# Revit family: Drinking_Fountain_Bottle_Filler-Murdock-H2O-To-Go-A191.8-BF_Series
name_source: partatom
category: Plumbing Fixtures
units: mm (PartAtom-declared; Revit-internal decimal feet)

## family parameters
Cut with Voids When Loaded = No
Host = Face
OmniClass Number = 23.65.70.14.11
OmniClass Title = Drinking Fountains/Coolers
Part Type = Normal
Room Calculation Point = No
Round Connector Dimension = Use Diameter
Shared = Yes

## types (6) — shared parameters
ADA = Yes
ADA Compliant = Yes
Amps = 4 A
Assembly Code = D2010800
Basin Material = Metal-Murdock-Stainless Steel
Bottle Filler Material = Stainless Steel-Murdock-Satin
CW Connection = Yes
CWFU = 1.5
Cabinet Material = Stainless Steel-Murdock-Brushed
Child ADA = No
Default Elevation = 0"
Description = Wall-Mounted, Square, Push Button Drinking Fountain with Wide Basin & H2O-to-Go!® Touchless Water Filling Station - In-Wall Refrigeration (8GPH), ADA, Stainless Steel
Finish = Metal-Murdock-18 Gage-Type 304-Bronze
Flow Rate = 1 GPM
GPH = 8.0
HW Connection = No
Height = 49 1/8"
IAPMO Compliance = Unit is certified to ANSI A117.1, Public Law 111-380 (NO-LEAD), CHSC 116875 and NSF/ANSI 61, Section 9.
Inlet Connection Diameter = 3/8"
Inlet Connection Height = 29 1/4"
Installation Instruction Link = https://www.murdockmfg.com
Installation Type = Wall Mounted
Length = 23 3/4"
Manufacturer = Murdock
Material = Metal-Murdock-Stainless Steel
Mounting Height = 27"
Mounting Height Constraint from Under Fountain = 27"
Product Documentation Link = https://www.murdockmfg.com
Product Page URL = https://www.murdockmfg.com
Pushbutton Material = Brass-Murdock-Chrome Plated
Shipping Weight = 130 lbs.
URL = http://www.murdockmfg.com
Vent Connection = No
WF1 - 1500 gallon capacity, NSF 42+53, 1 micron lead reduction filter = No
WF3 3000-Gallon Capacity, NSF 42+53, 1-Micron Lead Reduction Filter = No
WFU = 2
Warranty Information = Murdock Mfg.™ warrants that its products are free from defects in material or workmanship under normal use and service for a period of one year from date of shipment.
Waste Connection = Yes
Waste Connection Diameter = 1 1/4"
Waste Connection Height = 29 5/8"
Waste Connection Width = 4 1/4"
Water Pressure = 20-105 PSIG
Watts = 390 W
Width = 19"
cUPC Compliant = Yes
zero-valued in all types: HWFU

## per-type parameters (varying)
| type | -BCD Bottle Counter Display | 115v Plug-In Transformer | BF11 - Push Button Deck Mount H2O to Go!® Bottler Filler | BF12 - H2O-To-Go!® Sensor-Operated Water Refill Station | Bottle Filler Type | Bubbler Material | Type Comments |
| A191408F-BF11 | No | No | Yes | No | Bottle_Filler-Murdock-H2O-To-Go-BFI1-BF12_Series : BF11 | Rubber-Murdock-Santoprene | Flexible Bubbler Drinking Fountain and BottleFiller with Pushbutton Operation |
| A191408F-BF12 | No | Yes | No | Yes | Bottle_Filler-Murdock-H2O-To-Go-BFI1-BF12_Series : BF12 | Rubber-Murdock-Santoprene | Flexible Bubbler Drinking Fountain and BottleFiller with Sensor Operation |
| A191408F-BF12-BCD | Yes | Yes | No | Yes | Bottle_Filler-Murdock-H2O-To-Go-BFI1-BF12_Series : BF12-BCD | Rubber-Murdock-Santoprene | Flexible Bubbler Drinking Fountain and Bottle Filler with Sensor Operation and Bottle Counter Display |
| A191408S-BF11 | No | No | Yes | No | Bottle_Filler-Murdock-H2O-To-Go-BFI1-BF12_Series : BF11 | Stainless Steel-Murdock-Polished | Stainless Steel Drinking Fountain and BottleFiller with Pushbutton Operation |
| A191408S-BF12 | No | Yes | No | Yes | Bottle_Filler-Murdock-H2O-To-Go-BFI1-BF12_Series : BF12 | Stainless Steel-Murdock-Polished | Stainless Steel Bubbler Drinking Fountain and BottleFiller with Sensor Operation |
| A191408S-BF12-BCD | Yes | Yes | No | Yes | Bottle_Filler-Murdock-H2O-To-Go-BFI1-BF12_Series : BF12-BCD | Stainless Steel-Murdock-Polished | Stainless Steel Bubbler Drinking Fountain and Bottle Filler with Sensor Operation and Bottle Counter Display |

note: column(s) folded — value = type name in every type: Model

## geometry (parser evidence)
native form markers: Sweep x5
no freeform markers — native parametric forms only
